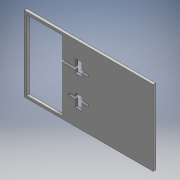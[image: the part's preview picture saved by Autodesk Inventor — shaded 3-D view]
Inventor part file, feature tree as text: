
AUTODESK INVENTOR PART (.ipt)
format: ipt  version: 2016 (Build 200138000, 138)  size: 141,312 bytes
history: native  units: mm
features: extrude x1, sketch x1
ambient origin geometry x8: Origin, YZ Plane, XZ Plane, XY Plane, X Axis, Y Axis, Z Axis, Center Point
bodies: Body1 (feature_tree)
feature tree (2):
  extrude  "Extrusion4"  Depth=59.0mm
  sketch  "Sketch1"  dims[d0=101.0mm d1=59.0mm d4=5.0mm d5=10.0mm d6=10.0mm d7=2.0mm d8=5.0mm d14=20.0mm d15=2.0mm d16=2.0mm d17=55.0mm d18=2.0mm d19=28.0mm d25=2.0mm d26=0.0mm]
